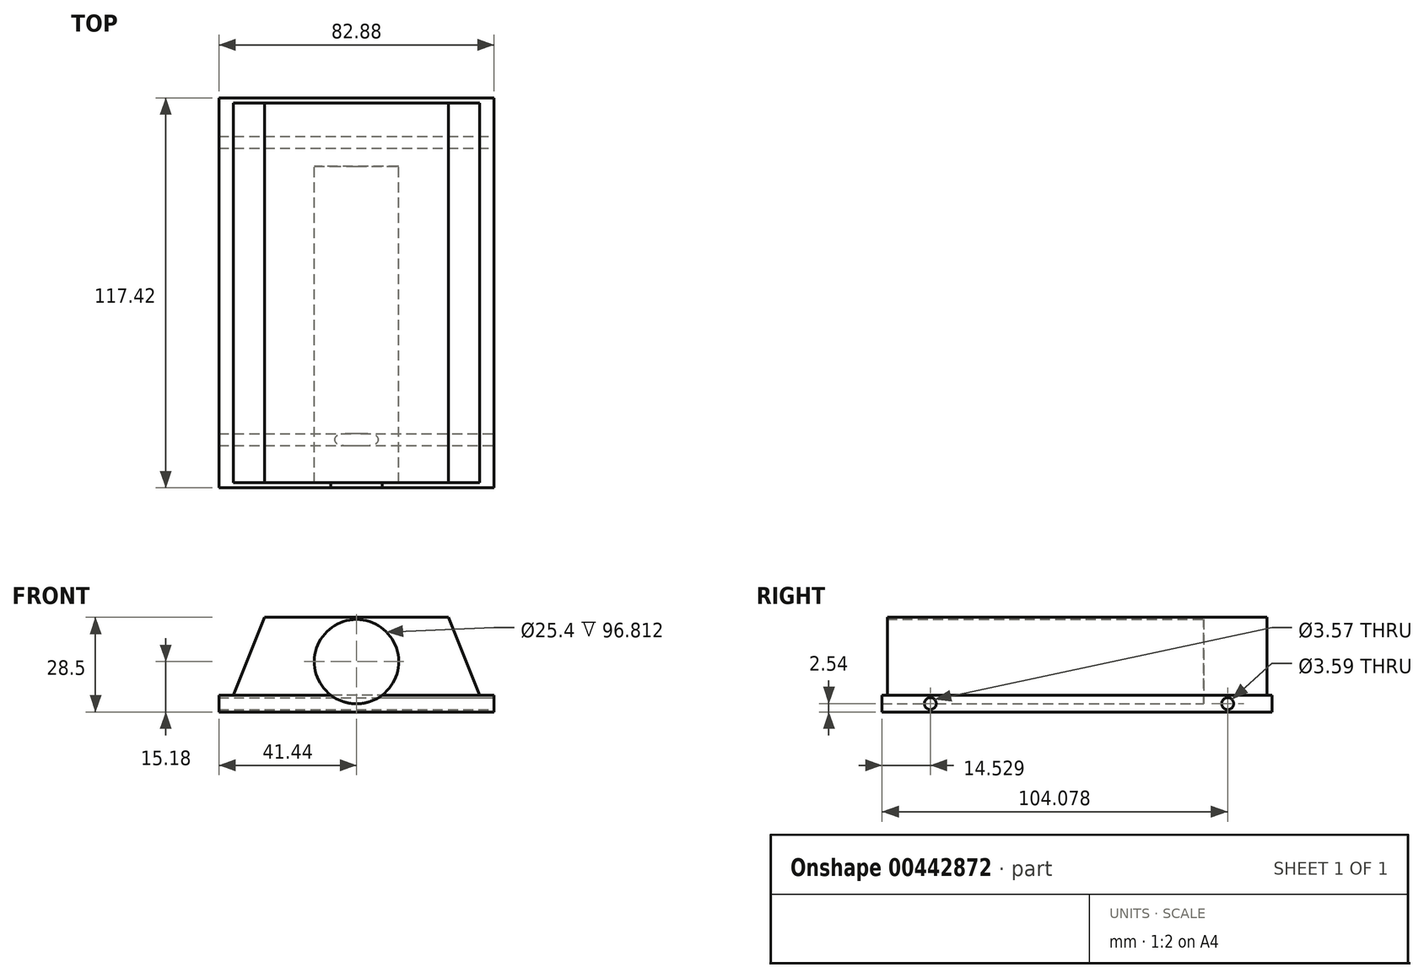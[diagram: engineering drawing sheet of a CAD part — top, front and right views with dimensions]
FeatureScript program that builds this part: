
annotation { "Feature Type Name" : "Feature", "Feature Type Description" : "" }
export const myFeature = defineFeature(function(context is Context, id is Id, definition is map)
    precondition{}
    {
        {
            var Q0;
            Q0=qCreatedBy(makeId("Front.planeOp"),FACE);
            var sketch = newSketch(context, id + "F0", { "sketchPlane" : qUnion([Q0])});
            skLineSegment(sketch, "E0", {"start": v(0, 0) * mm, "end": v(-38.1, 0) * mm});
            skLineSegment(sketch, "E1", {"start": v(-38.1, 0) * mm, "end": v(-27.73, 25.96) * mm});
            skLineSegment(sketch, "E2", {"start": v(-27.73, 25.96) * mm, "end": v(0, 25.96) * mm});
            skLineSegment(sketch, "E3.MirrorCS", {"start": v(0, 0) * mm, "end": v(38.1, 0) * mm});
            skLineSegment(sketch, "E4.MirrorCS", {"start": v(38.1, 0) * mm, "end": v(27.73, 25.96) * mm});
            skLineSegment(sketch, "E5.MirrorCS", {"start": v(27.73, 25.96) * mm, "end": v(0, 25.96) * mm});
            skSolve(sketch);
        }
        {
            var Q0;
            Q0 = qSketchRegion(id + "F0", true);
            extrude(context, id + "F1", {"entities" : qUnion([Q0]), "endBound" : BoundingType.SYMMETRIC, "depth" : 114.3 * mm});
        }
        {
            var Q0;
            Q0=qCreatedBy(makeId("Top.planeOp"),FACE);
            var sketch = newSketch(context, id + "F2", { "sketchPlane" : qUnion([Q0])});
            skLineSegment(sketch, "E6", {"start": v(-41.44, 0) * mm, "end": v(-41.44, 58.71) * mm});
            skLineSegment(sketch, "E7", {"start": v(-41.44, 58.71) * mm, "end": v(0, 58.71) * mm});
            skLineSegment(sketch, "E8.MirrorCS", {"start": v(41.44, 58.71) * mm, "end": v(0, 58.71) * mm});
            skLineSegment(sketch, "E9.MirrorCS", {"start": v(-41.44, 0) * mm, "end": v(-41.44, -58.71) * mm});
            skLineSegment(sketch, "E10.MirrorCS", {"start": v(41.44, 0) * mm, "end": v(41.44, 58.71) * mm});
            skLineSegment(sketch, "E11.MirrorCS", {"start": v(41.44, 0) * mm, "end": v(41.44, -58.71) * mm});
            skLineSegment(sketch, "E12.MirrorCS", {"start": v(-41.44, -58.71) * mm, "end": v(0, -58.71) * mm});
            skLineSegment(sketch, "E13.MirrorCS", {"start": v(41.44, -58.71) * mm, "end": v(0, -58.71) * mm});
            skSolve(sketch);
        }
        {
            var Q0;
            Q0 = qSketchRegion(id + "F2", true);
            extrude(context, id + "F3", {"entities" : qUnion([Q0]), "operationType" : NewBodyOperationType.ADD, "endBound" : BoundingType.SYMMETRIC, "depth" : 5.08 * mm});
        }
        {
            var Q0;
            Q0=qCreatedBy(makeId("Front.planeOp"),FACE);
            var sketch = newSketch(context, id + "F4", { "sketchPlane" : qUnion([Q0])});
            skCircle(sketch, "E14", {"center": v(0, 12.64) * mm, "radius": 12.7 * mm});
            skSolve(sketch);
        }
        {
            var Q0;
            Q0 = qSketchRegion(id + "F4", true);
            extrude(context, id + "F5", {"entities" : qUnion([Q0]), "operationType" : NewBodyOperationType.REMOVE, "depth" : 98.8 * mm, "hasSecondDirection" : true, "secondDirectionOppositeDirection" : true, "secondDirectionDepth" : 38.1 * mm});
        }
        {
            var Q0;
            Q0=qCreatedBy(makeId("Right.planeOp"),FACE);
            var sketch = newSketch(context, id + "F6", { "sketchPlane" : qUnion([Q0])});
            skCircle(sketch, "E15", {"center": v(-44.18, 0) * mm, "radius": 1.79 * mm});
            skCircle(sketch, "E16", {"center": v(45.37, 0) * mm, "radius": 1.8 * mm});
            skSolve(sketch);
        }
        {
            var Q0;
            Q0 = qSketchRegion(id + "F6", true);
            extrude(context, id + "F7", {"entities" : qUnion([Q0]), "operationType" : NewBodyOperationType.REMOVE, "endBound" : BoundingType.SYMMETRIC, "oppositeDirection" : true, "depth" : 99.06 * mm});
        }
    });
